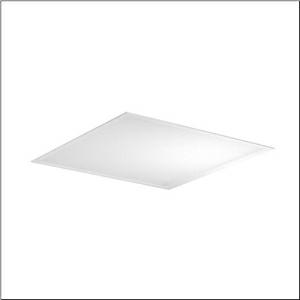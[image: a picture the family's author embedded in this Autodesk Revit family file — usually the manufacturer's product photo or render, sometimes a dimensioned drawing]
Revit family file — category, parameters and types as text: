
# Revit family: apollon_r__31_square_51mp12wd2342_f4b0
name_source: partatom
category: Lighting Fixtures
units: mm (PartAtom-declared; Revit-internal decimal feet)

## family parameters
Cut with Voids When Loaded = No
Host = Face
Light Source = No
Part Type = Normal
Room Calculation Point = No
Round Connector Dimension = Use Diameter
Shared = No

## types (1)
- Apollon® 31 square (1 x LED, 3600 lm, 27.5 W, 3000K)
    Apparent Load = 28 VA
    CIE Flux Codes = 61 87 97 100 100
    Color Rendering = 80
    Color Temperature = 3000K
    Default Elevation = 1800 mm
    Description = Apollon® 31 square, office luminaire, primary optical cover: micro prismatic cover, of PMMA, CAT 2 (L<= 3000cd/m²), light emission: direct distribution, primary light characteristic: symmetric, installation type: lay-in mounting, LED, rated luminous flux: 3.600lm, luminous efficacy: 130lm/W, light colour: 830, colour temperature: 3000K, control gear: DALI 2, Multilumen, with terminal, 5-pole, mains connection: 220..240V, AC/DC, 0/50..60Hz, rated input power: 27.5W, housing, of aluminium, traffic white (RAL 9016), module: M600, length: 595mm, width: 595mm, height: 62mm, recess depth: 180mm, housing upper side, of sheet steel, coated, protection rating (complete): IP20, protection rating (on room side): IP40, insulation class (complete): insulation class II (safety insulation), certification: CE, ENEC, impact resistance: IK03, permissible operating ambient temperature: -20..+40°C, permissible storage temperature: -20..+60°C, standard: EN 60598-2-22, packaging unit: 1 piece
    Height = 0 mm  [stored 0 ft]
    Lamp = 1 x LED
    Lamp Light Flux = 3600 lm
    Lamp Power = 27.5 W
    Lamp count = 1
    Length = 595 mm
    Luminous efficacy = 131 lm/W
    Manufacturer = Siteco
    ModVariant = No
    Model = 51MP12WD2342
    Mounting Place = Ceiling
    Mounting Type = Recessed
    Number of Poles = 1
    OnlyDefault = Yes
    Power Factor = 1
    Product Name = Apollon® 31 square
    Product group = office luminaire | ceiling recessed
    ProductGroupID = 401
    Protection Class = Protection class II
    Protection Degree = IP 20
    RLX_Detail_Level = 1
    RLX_Emergency_Light_Flux = 0 lm
    RLX_Emergency_Type = 0
    RLX_Emergency_Type_DB = No
    RlxData = <blob elided: 12569 chars, md5=6d6d9ec2>
    Socket = socket
    Standby Power = 0 W
    System Light Flux = 3600 lm
    System Power = 28 W
    Type Comments = Product without accessories
    Type Image = l_1291035.jpg
    URL = http://relux.com
    VarID = ---
    Voltage = 0 V
    Weight = 0.00 kg
    Width = 595 mm

note: [stored X ft] marks values corroborated as IEEE doubles in the binary element streams (Revit-internal decimal feet)

## geometry (parser evidence)
native form markers: Sweep x10
no freeform markers — native parametric forms only
